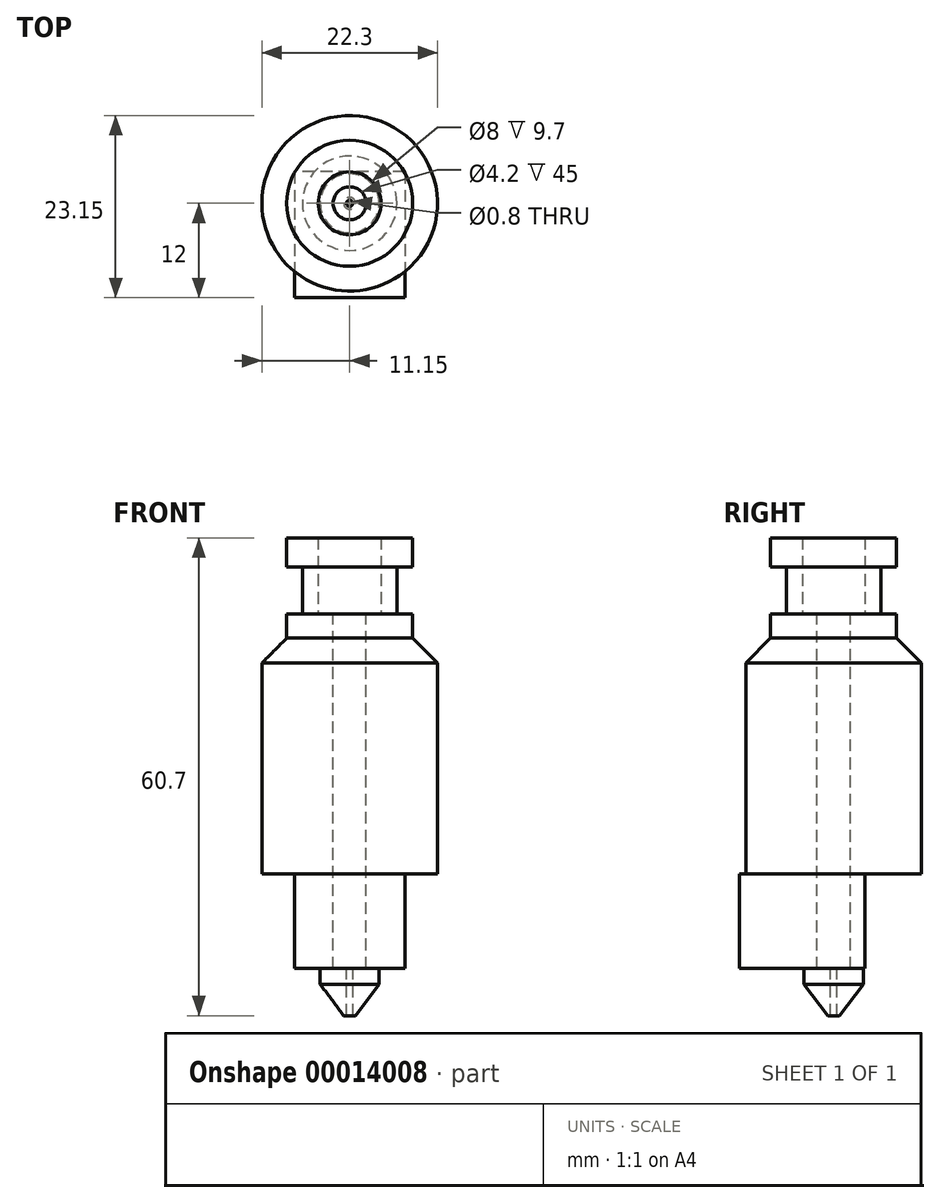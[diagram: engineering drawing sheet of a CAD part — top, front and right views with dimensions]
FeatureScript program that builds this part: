
annotation { "Feature Type Name" : "Feature", "Feature Type Description" : "" }
export const myFeature = defineFeature(function(context is Context, id is Id, definition is map)
    precondition{}
    {
        {
            var Q0;
            Q0=qCreatedBy(makeId("Top.planeOp"),FACE);
            var sketch = newSketch(context, id + "F0", { "sketchPlane" : qUnion([Q0])});
            skCircle(sketch, "E0", {"center": v(0, 0) * mm, "radius": 8 * mm});
            skCircle(sketch, "E1", {"center": v(0, 0) * mm, "radius": 4 * mm});
            skSolve(sketch);
        }
        {
            var Q0;
            Q0=qSketchRegion(id+"F0",true);
            extrude(context, id + "F1", {"entities" : qUnion([Q0]), "depth" : 3.7 * mm});
        }
        {
            var Q0;
            Q0=makeQuery(id+"F1.opExtrude","CAP_FACE",FACE,{"disambiguationData":[OSD([sQuery(id+"F0.wireOp",EDGE,"E0"),sQuery(id+"F0.wireOp",EDGE,"E1")])],"isStart":true});
            var sketch = newSketch(context, id + "F2", { "sketchPlane" : qUnion([Q0])});
            skCircle(sketch, "E2", {"center": v(0, 0) * mm, "radius": 6 * mm});
            skSolve(sketch);
        }
        {
            var Q0;
            Q0=makeQuery(id+"F2.imprint","IMPRINT",FACE,{"disambiguationData":[TD([[makeQuery(id+"F2.imprint","IMPRINT",EDGE,{"derivedFrom":sQuery(id+"F2.wireOp",EDGE,"E2")}),1.0]])]});
            extrude(context, id + "F3", {"entities" : qUnion([Q0]), "operationType" : NewBodyOperationType.ADD, "depth" : 6 * mm});
        }
        {
            var Q0;
            Q0=makeQuery(id+"F3.opExtrude","CAP_FACE",FACE,{"disambiguationData":[OSD([sQuery(id+"F0.wireOp",EDGE,"E1"),sQuery(id+"F2.wireOp",EDGE,"E2")])],"isStart":false});
            var sketch = newSketch(context, id + "F4", { "sketchPlane" : qUnion([Q0])});
            skCircle(sketch, "E3", {"center": v(0, 0) * mm, "radius": 2.1 * mm});
            skCircle(sketch, "E4.0", {"center": v(0, 0) * mm, "radius": 8 * mm});
            skSolve(sketch);
        }
        {
            var Q0;
            Q0=qSketchRegion(id+"F4",true);
            extrude(context, id + "F5", {"entities" : qUnion([Q0]), "operationType" : NewBodyOperationType.ADD, "depth" : 3 * mm});
        }
        {
            var Q0;
            Q0=makeQuery(id+"F5.opExtrude","CAP_FACE",FACE,{"disambiguationData":[OSD([sQuery(id+"F4.wireOp",EDGE,"E3"),sQuery(id+"F4.wireOp",EDGE,"E4.0")])],"isStart":false});
            var sketch = newSketch(context, id + "F6", { "sketchPlane" : qUnion([Q0])});
            skCircle(sketch, "E5", {"center": v(0, 0) * mm, "radius": 11.15 * mm});
            skSolve(sketch);
        }
        {
            var Q0;
            Q0=makeQuery(id+"F6.imprint","IMPRINT",FACE,{"disambiguationData":[TD([[makeQuery(id+"F6.imprint","IMPRINT",EDGE,{"derivedFrom":sQuery(id+"F6.wireOp",EDGE,"E5")}),1.0]])]});
            var Q1;
            Q1=makeQuery(id+"F6.imprint","IMPRINT",FACE,{"disambiguationData":[TD([[makeQuery(id+"F6.imprint","IMPRINT",EDGE,{"derivedFrom":makeQuery(id+"F5.opExtrude","CAP_EDGE",EDGE,{"disambiguationData":[OSD([sQuery(id+"F4.wireOp",EDGE,"E3")])],"isStart":false})}),-1.0]])]});
            extrude(context, id + "F7", {"entities" : qUnion([Q0, Q1]), "operationType" : NewBodyOperationType.ADD, "depth" : 30 * mm});
        }
        {
            var Q0;
            Q0=makeQuery(id+"F7.opExtrude","CAP_EDGE",EDGE,{"disambiguationData":[OSD([sQuery(id+"F6.wireOp",EDGE,"E5")])],"isStart":true});
            chamfer(context, id + "F8", {"entities" : qUnion([Q0]), "width" : 3.2 * mm});
        }
        {
            var Q0;
            Q0=makeQuery(id+"F7.opExtrude","CAP_FACE",FACE,{"disambiguationData":[OSD([sQuery(id+"F4.wireOp",EDGE,"E3"),sQuery(id+"F6.wireOp",EDGE,"E5")])],"isStart":false});
            var sketch = newSketch(context, id + "F9", { "sketchPlane" : qUnion([Q0])});
            skLineSegment(sketch, "E6.bottom", {"start": v(7, -4) * mm, "end": v(-7, -4) * mm});
            skLineSegment(sketch, "E6.top", {"start": v(7, 12) * mm, "end": v(-7, 12) * mm});
            skLineSegment(sketch, "E6.left", {"start": v(7, -4) * mm, "end": v(7, 12) * mm});
            skLineSegment(sketch, "E6.right", {"start": v(-7, -4) * mm, "end": v(-7, 12) * mm});
            skSolve(sketch);
        }
        {
            var Q0;
            {var subQ3=sQuery(id+"F9.wireOp",EDGE,"E6.top");Q0=makeQuery(id+"F9.imprint","IMPRINT",FACE,{"disambiguationData":[TD([[makeQuery(id+"F9.imprint","IMPRINT",EDGE,{"derivedFrom":subQ3}),1.0]])]});}
            var Q1;
            {var subQ5=sQuery(id+"F9.wireOp",EDGE,"E6.bottom");Q1=makeQuery(id+"F9.imprint","IMPRINT",FACE,{"disambiguationData":[TD([[makeQuery(id+"F9.imprint","IMPRINT",EDGE,{"derivedFrom":subQ5}),-1.0]])]});}
            extrude(context, id + "F10", {"entities" : qUnion([Q0, Q1]), "operationType" : NewBodyOperationType.ADD, "depth" : 12 * mm});
        }
        {
            var Q0;
            Q0=makeQuery(id+"F10.opExtrude","CAP_FACE",FACE,{"disambiguationData":[OSD([sQuery(id+"F4.wireOp",EDGE,"E3"),sQuery(id+"F9.wireOp",EDGE,"E6.bottom"),sQuery(id+"F9.wireOp",EDGE,"E6.top"),sQuery(id+"F9.wireOp",EDGE,"E6.left"),sQuery(id+"F9.wireOp",EDGE,"E6.right")])],"isStart":false});
            var sketch = newSketch(context, id + "F11", { "sketchPlane" : qUnion([Q0])});
            skCircle(sketch, "E7", {"center": v(0, 0) * mm, "radius": 3.75 * mm});
            skCircle(sketch, "E8", {"center": v(0, 0) * mm, "radius": 0.4 * mm});
            skSolve(sketch);
        }
        {
            var Q0;
            Q0=qSketchRegion(id+"F11",true);
            extrude(context, id + "F12", {"entities" : qUnion([Q0]), "operationType" : NewBodyOperationType.ADD, "depth" : 6 * mm});
        }
        {
            var Q0;
            Q0=makeQuery(id+"F12.opExtrude","CAP_EDGE",EDGE,{"disambiguationData":[OSD([sQuery(id+"F11.wireOp",EDGE,"E7")])],"isStart":false});
            chamfer(context, id + "F13", {"entities" : qUnion([Q0]), "chamferType" : ChamferType.TWO_OFFSETS, "width1" : 3 * mm, "oppositeDirection" : false, "width2" : 4 * mm, "tangentPropagation" : true});
        }
    });
